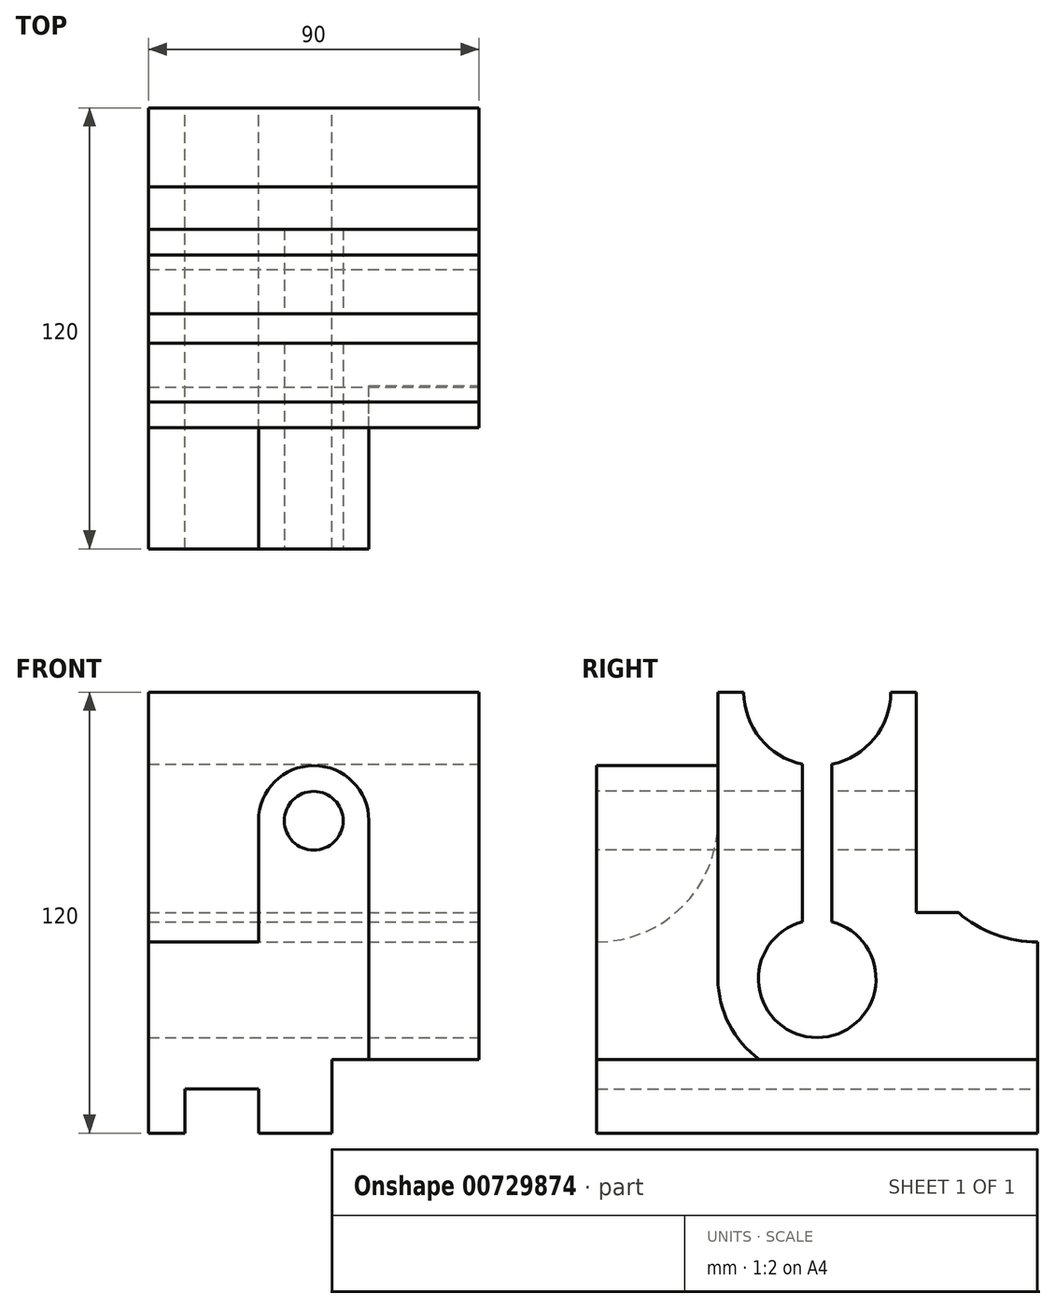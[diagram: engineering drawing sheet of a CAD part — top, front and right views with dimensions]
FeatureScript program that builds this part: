
annotation { "Feature Type Name" : "Feature", "Feature Type Description" : "" }
export const myFeature = defineFeature(function(context is Context, id is Id, definition is map)
    precondition{}
    {
        {
            assignVariable(context, id + "F0", {"name" : "x", "anyValue" : 15});
        }
        {
            assignVariable(context, id + "F1", {"name" : "y", "anyValue" : 27});
        }
        {
            var Q0;
            Q0=qCreatedBy(makeId("Right.planeOp"),FACE);
            var sketch = newSketch(context, id + "F2", { "sketchPlane" : qUnion([Q0])});
            skLineSegment(sketch, "E0.bottom", {"start": v(-60, -42) * mm, "end": v(60, -42) * mm});
            skLineSegment(sketch, "E0.top", {"start": v(-60, 78) * mm, "end": v(-20, 78) * mm});
            skLineSegment(sketch, "E0.left", {"start": v(-60, -42) * mm, "end": v(-60, 78) * mm});
            skLineSegment(sketch, "E0.right", {"start": v(60, -42) * mm, "end": v(60, 10) * mm});
            skLineSegment(sketch, "E1", {"start": v(0, 0) * mm, "end": v(0, 45.9) * mm, "construction": true});
            skArc(sketch, "E2", {"start": v(-20, 78) * mm, "mid": v(-15.5, 65.35) * mm, "end": v(-4, 58.4) * mm});
            skArc(sketch, "E3", {"start": v(-4, 15.5) * mm, "mid": v(0, -16) * mm, "end": v(4, 15.5) * mm});
            skLineSegment(sketch, "E4", {"start": v(4, 15.5) * mm, "end": v(4, 58.4) * mm});
            skLineSegment(sketch, "E5.MirrorCS", {"start": v(-4, 15.5) * mm, "end": v(-4, 58.4) * mm});
            skLineSegment(sketch, "E6.trimOffspring", {"start": v(20, 78) * mm, "end": v(27, 78) * mm});
            skArc(sketch, "E7.trimOffspring", {"start": v(4, 58.4) * mm, "mid": v(15.5, 65.35) * mm, "end": v(20, 78) * mm});
            skLineSegment(sketch, "E8", {"start": v(27, 78) * mm, "end": v(27, 18) * mm});
            skLineSegment(sketch, "E9", {"start": v(27, 18) * mm, "end": v(38.46, 18) * mm});
            skLineSegment(sketch, "E10.MirrorCS", {"start": v(-27, 78) * mm, "end": v(-27, 0) * mm});
            skLineSegment(sketch, "E11", {"start": v(0, 0) * mm, "end": v(43.64, 0) * mm, "construction": true});
            skArc(sketch, "E12", {"start": v(38.46, 18) * mm, "mid": v(48.51, 12.06) * mm, "end": v(60, 10) * mm});
            skPoint(sketch, "E13.orphan", {"position": v(60, 18) * mm});
            skPoint(sketch, "E14.orphan", {"position": v(60, 78) * mm});
            skLineSegment(sketch, "E15.0", {"start": v(-60, -22) * mm, "end": v(60, -22) * mm});
            skArc(sketch, "E16", {"start": v(-27, 0) * mm, "mid": v(-24, -12.38) * mm, "end": v(-15.65, -22) * mm});
            skSolve(sketch);
        }
        {
            var Q0;
            Q0 = qSketchRegion(id + "F2", true);
            extrude(context, id + "F3", {"entities" : qUnion([Q0]), "oppositeDirection" : true, "depth" : 90 * mm, "offsetDistance" : 25 * mm});
        }
        {
            var Q0;
            {var subQ4=sQuery(id+"F2.wireOp",EDGE,"E0.bottom");Q0=makeQuery(id+"F2.imprint","IMPRINT",FACE,{"disambiguationData":[TD([[makeQuery(id+"F2.imprint","IMPRINT",EDGE,{"derivedFrom":subQ4}),1.0]])]});}
            extrude(context, id + "F4", {"entities" : qUnion([Q0]), "operationType" : NewBodyOperationType.REMOVE, "oppositeDirection" : true, "depth" : (90 - 20 - 20 - 10) * mm, "offsetDistance" : 25 * mm});
        }
        {
            var Q0;
            {var subQ4=sQuery(id+"F2.wireOp",EDGE,"E10.MirrorCS");Q0=makeQuery(id+"F2.imprint","IMPRINT",FACE,{"disambiguationData":[TD([[makeQuery(id+"F2.imprint","IMPRINT",EDGE,{"derivedFrom":subQ4}),-1.0]])]});}
            extrude(context, id + "F5", {"entities" : qUnion([Q0]), "operationType" : NewBodyOperationType.REMOVE, "oppositeDirection" : true, "depth" : (90 - 45 - getVariable(context, 'x')) * mm, "offsetDistance" : 25 * mm});
        }
        {
            var Q0;
            Q0=makeQuery(id+"F3.opExtrude","SWEPT_FACE",FACE,{"disambiguationData":[OSD([sQuery(id+"F2.wireOp",EDGE,"E0.right")])]});
            var sketch = newSketch(context, id + "F6", { "sketchPlane" : qUnion([Q0])});
            skLineSegment(sketch, "E17.bottom", {"start": v(80, -42) * mm, "end": v(60, -42) * mm});
            skLineSegment(sketch, "E17.top", {"start": v(80, -30) * mm, "end": v(60, -30) * mm});
            skLineSegment(sketch, "E17.left", {"start": v(80, -42) * mm, "end": v(80, -30) * mm});
            skLineSegment(sketch, "E17.right", {"start": v(60, -42) * mm, "end": v(60, -30) * mm});
            skSolve(sketch);
        }
        {
            var Q0;
            Q0 = qSketchRegion(id + "F6", true);
            extrude(context, id + "F7", {"entities" : qUnion([Q0]), "operationType" : NewBodyOperationType.REMOVE, "endBound" : BoundingType.THROUGH_ALL, "oppositeDirection" : true, "depth" : 25 * mm, "offsetDistance" : 25 * mm});
        }
        {
            var Q0;
            Q0=makeQuery(id+"F3.opExtrude","SWEPT_FACE",FACE,{"disambiguationData":[OSD([sQuery(id+"F2.wireOp",EDGE,"E0.left")])]});
            var sketch = newSketch(context, id + "F8", { "sketchPlane" : qUnion([Q0])});
            skLineSegment(sketch, "E18", {"start": v(-45, 0) * mm, "end": v(-45, 43) * mm, "construction": true});
            skCircle(sketch, "E19", {"center": v(-45, 43) * mm, "radius": 8 * mm});
            skCircle(sketch, "E20", {"center": v(-45, 43) * mm, "radius": 15 * mm});
            skLineSegment(sketch, "E21", {"start": v(-60, 43) * mm, "end": v(-60, 10) * mm});
            skLineSegment(sketch, "E22", {"start": v(-60, 10) * mm, "end": v(-90, 10) * mm});
            skLineSegment(sketch, "E23.0", {"start": v(-30, 43) * mm, "end": v(-30, 78) * mm});
            skLineSegment(sketch, "E24.0", {"start": v(-90, 78) * mm, "end": v(-30, 78) * mm});
            skLineSegment(sketch, "E25.0", {"start": v(-90, 10) * mm, "end": v(-90, 78) * mm});
            skPoint(sketch, "E26.orphan", {"position": v(-30, -22) * mm});
            skPoint(sketch, "E27.orphan", {"position": v(-90, -42) * mm});
            skSolve(sketch);
        }
        {
            var Q0;
            {var subQ1=sQuery(id+"F8.wireOp",EDGE,"E21");Q0=makeQuery(id+"F8.imprint","IMPRINT",FACE,{"disambiguationData":[TD([[makeQuery(id+"F8.imprint","IMPRINT",EDGE,{"derivedFrom":subQ1}),-1.0]])]});}
            extrude(context, id + "F9", {"entities" : qUnion([Q0]), "operationType" : NewBodyOperationType.REMOVE, "oppositeDirection" : true, "depth" : (60 - getVariable(context, 'y')) * mm, "offsetDistance" : 25 * mm});
        }
        {
            var Q0;
            Q0=makeQuery(id+"F8.imprint","IMPRINT",FACE,{"disambiguationData":[TD([[makeQuery(id+"F8.imprint","IMPRINT",EDGE,{"derivedFrom":sQuery(id+"F8.wireOp",EDGE,"E19")}),1.0]])]});
            extrude(context, id + "F10", {"entities" : qUnion([Q0]), "operationType" : NewBodyOperationType.REMOVE, "endBound" : BoundingType.THROUGH_ALL, "oppositeDirection" : true, "depth" : 25 * mm, "offsetDistance" : 25 * mm});
        }
        {
            var Q0;
            Q0=makeQuery(id+"F3.opExtrude","CAP_FACE",FACE,{"disambiguationData":[OSD([sQuery(id+"F2.wireOp",EDGE,"E0.bottom"),sQuery(id+"F2.wireOp",EDGE,"E0.top"),sQuery(id+"F2.wireOp",EDGE,"E0.left"),sQuery(id+"F2.wireOp",EDGE,"E0.right"),sQuery(id+"F2.wireOp",EDGE,"E2"),sQuery(id+"F2.wireOp",EDGE,"E3"),sQuery(id+"F2.wireOp",EDGE,"E4"),sQuery(id+"F2.wireOp",EDGE,"E5.MirrorCS"),sQuery(id+"F2.wireOp",EDGE,"E6.trimOffspring"),sQuery(id+"F2.wireOp",EDGE,"E7.trimOffspring"),sQuery(id+"F2.wireOp",EDGE,"E8"),sQuery(id+"F2.wireOp",EDGE,"E9"),sQuery(id+"F2.wireOp",EDGE,"E12")])],"isStart":false});
            var sketch = newSketch(context, id + "F11", { "sketchPlane" : qUnion([Q0])});
            skPoint(sketch, "E28.0", {"position": v(60, 43) * mm});
            skArc(sketch, "E29", {"start": v(27, 43) * mm, "mid": v(36.67, 19.67) * mm, "end": v(60, 10) * mm});
            skLineSegment(sketch, "E30.0", {"start": v(27, 10) * mm, "end": v(27, 43) * mm});
            skLineSegment(sketch, "E31.0", {"start": v(27, 10) * mm, "end": v(60, 10) * mm});
            skPoint(sketch, "E32.orphan", {"position": v(27, 78) * mm});
            skSolve(sketch);
        }
        {
            var Q0;
            Q0 = qSketchRegion(id + "F11", true);
            var Q1;
            Q1=makeQuery(id+"F9.boolean.opBoolean","COPY",FACE,{"derivedFrom":makeQuery(id+"F9.opExtrude","SWEPT_FACE",FACE,{"disambiguationData":[OSD([sQuery(id+"F8.wireOp",EDGE,"E21")])]})});
            extrude(context, id + "F12", {"entities" : qUnion([Q0]), "operationType" : NewBodyOperationType.ADD, "endBound" : BoundingType.UP_TO_SURFACE, "oppositeDirection" : true, "depth" : 25 * mm, "endBoundEntityFace" : qUnion([Q1]), "offsetDistance" : 25 * mm});
        }
    });
